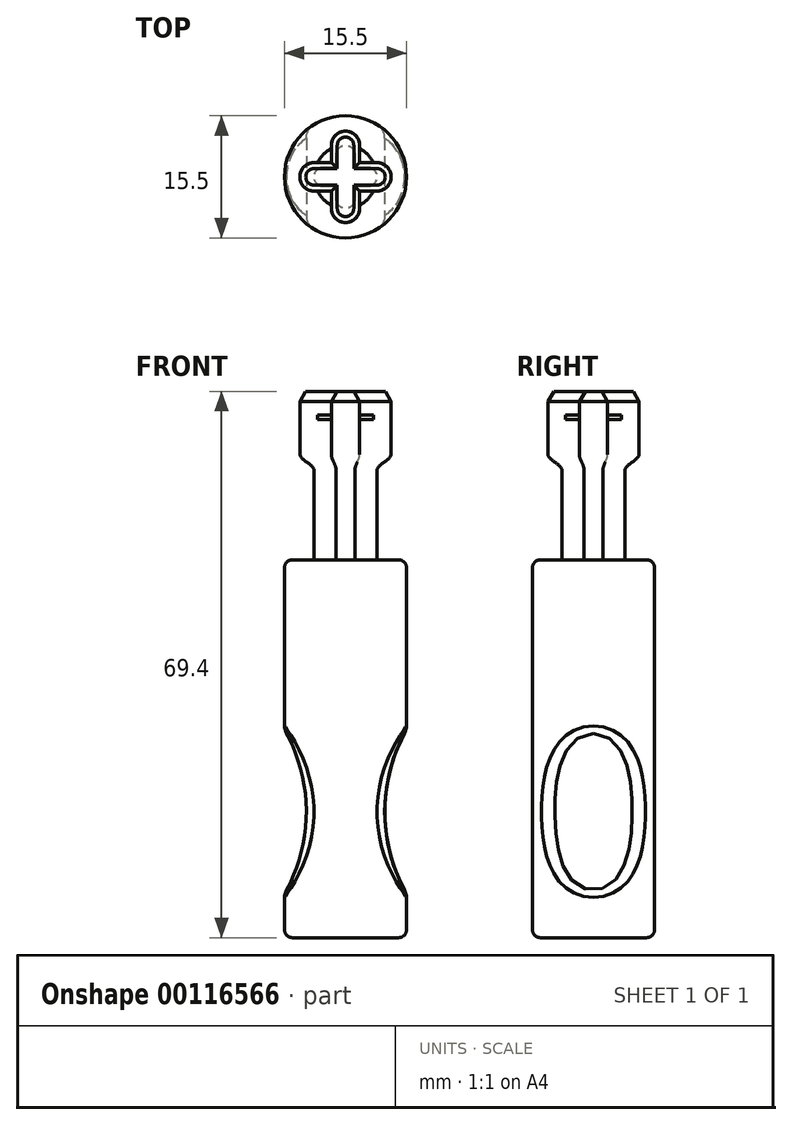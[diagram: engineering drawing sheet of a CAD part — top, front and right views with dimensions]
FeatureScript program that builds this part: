
annotation { "Feature Type Name" : "Feature", "Feature Type Description" : "" }
export const myFeature = defineFeature(function(context is Context, id is Id, definition is map)
    precondition{}
    {
        {
            var Q0;
            Q0=qCreatedBy(makeId("Top.planeOp"),FACE);
            var sketch = newSketch(context, id + "F0", { "sketchPlane" : qUnion([Q0])});
            skCircle(sketch, "E0", {"center": v(0, 0) * mm, "radius": 7.75 * mm});
            skSolve(sketch);
        }
        {
            var Q0;
            Q0=makeQuery(id+"F0.imprint","IMPRINT",FACE,{"disambiguationData":[TD([[makeQuery(id+"F0.imprint","IMPRINT",EDGE,{"derivedFrom":sQuery(id+"F0.wireOp",EDGE,"E0")}),1.0]])]});
            extrude(context, id + "F1", {"entities" : qUnion([Q0]), "depth" : 48 * mm});
        }
        {
            var Q0;
            Q0=makeQuery(id+"F1.opExtrude","CAP_FACE",FACE,{"disambiguationData":[OSD([sQuery(id+"F0.wireOp",EDGE,"E0")])],"isStart":false});
            var sketch = newSketch(context, id + "F2", { "sketchPlane" : qUnion([Q0])});
            skLineSegment(sketch, "E1", {"start": v(2.8, 1.2) * mm, "end": v(1.2, 1.2) * mm});
            skLineSegment(sketch, "E2", {"start": v(1.2, 1.2) * mm, "end": v(1.2, 2.8) * mm});
            skLineSegment(sketch, "E3", {"start": v(-1.2, 2.8) * mm, "end": v(-1.2, 1.2) * mm});
            skLineSegment(sketch, "E4", {"start": v(-1.2, 1.2) * mm, "end": v(-2.8, 1.2) * mm});
            skLineSegment(sketch, "E5", {"start": v(-2.8, -1.2) * mm, "end": v(-1.2, -1.2) * mm});
            skLineSegment(sketch, "E6", {"start": v(-1.2, -1.2) * mm, "end": v(-1.2, -2.8) * mm});
            skLineSegment(sketch, "E7", {"start": v(1.2, -2.8) * mm, "end": v(1.2, -1.2) * mm});
            skLineSegment(sketch, "E8", {"start": v(1.2, -1.2) * mm, "end": v(2.8, -1.2) * mm});
            skArc(sketch, "E9", {"start": v(2.8, 1.2) * mm, "mid": v(4, 0) * mm, "end": v(2.8, -1.2) * mm});
            skArc(sketch, "E10", {"start": v(1.2, 2.8) * mm, "mid": v(0, 4) * mm, "end": v(-1.2, 2.8) * mm});
            skArc(sketch, "E11", {"start": v(-2.8, 1.2) * mm, "mid": v(-4, 0) * mm, "end": v(-2.8, -1.2) * mm});
            skArc(sketch, "E12", {"start": v(-1.2, -2.8) * mm, "mid": v(0, -4) * mm, "end": v(1.2, -2.8) * mm});
            skLineSegment(sketch, "E13", {"start": v(0, 2.8) * mm, "end": v(0, -2.8) * mm, "construction": true});
            skLineSegment(sketch, "E14", {"start": v(-2.8, 0) * mm, "end": v(2.8, 0) * mm, "construction": true});
            skPoint(sketch, "E15", {"position": v(0, 0) * mm});
            skSolve(sketch);
        }
        {
            var Q0;
            Q0=makeQuery(id+"F2.imprint","IMPRINT",FACE,{"disambiguationData":[TD([[makeQuery(id+"F2.imprint","IMPRINT",EDGE,{"derivedFrom":sQuery(id+"F2.wireOp",EDGE,"E1")}),1.0]])]});
            extrude(context, id + "F3", {"entities" : qUnion([Q0]), "operationType" : NewBodyOperationType.ADD, "depth" : 11.4 * mm});
        }
        {
            var Q0;
            Q0=makeQuery(id+"F3.opExtrude","CAP_FACE",FACE,{"disambiguationData":[OSD([sQuery(id+"F2.wireOp",EDGE,"E1"),sQuery(id+"F2.wireOp",EDGE,"E2"),sQuery(id+"F2.wireOp",EDGE,"E3"),sQuery(id+"F2.wireOp",EDGE,"E4"),sQuery(id+"F2.wireOp",EDGE,"E5"),sQuery(id+"F2.wireOp",EDGE,"E6"),sQuery(id+"F2.wireOp",EDGE,"E7"),sQuery(id+"F2.wireOp",EDGE,"E8"),sQuery(id+"F2.wireOp",EDGE,"E9"),sQuery(id+"F2.wireOp",EDGE,"E10"),sQuery(id+"F2.wireOp",EDGE,"E11"),sQuery(id+"F2.wireOp",EDGE,"E12")])],"isStart":false});
            cPlane(context, id + "F4", {"entities" : qUnion([Q0]), "cplaneType" : CPlaneType.OFFSET, "offset" : 2 * mm, "width" : 150 * mm, "height" : 150 * mm});
        }
        {
            var Q0;
            Q0=qCreatedBy(id+"F4.planeOp",FACE);
            var sketch = newSketch(context, id + "F5", { "sketchPlane" : qUnion([Q0])});
            skLineSegment(sketch, "E16", {"start": v(4, 1.8) * mm, "end": v(1.8, 1.8) * mm});
            skLineSegment(sketch, "E17", {"start": v(1.8, 1.8) * mm, "end": v(1.8, 4) * mm});
            skLineSegment(sketch, "E18", {"start": v(-1.8, 4) * mm, "end": v(-1.8, 1.8) * mm});
            skLineSegment(sketch, "E19", {"start": v(-1.8, 1.8) * mm, "end": v(-4, 1.8) * mm});
            skLineSegment(sketch, "E20", {"start": v(-4, -1.8) * mm, "end": v(-1.8, -1.8) * mm});
            skLineSegment(sketch, "E21", {"start": v(-1.8, -1.8) * mm, "end": v(-1.8, -4) * mm});
            skLineSegment(sketch, "E22", {"start": v(1.8, -4) * mm, "end": v(1.8, -1.8) * mm});
            skLineSegment(sketch, "E23", {"start": v(1.8, -1.8) * mm, "end": v(4, -1.8) * mm});
            skArc(sketch, "E24", {"start": v(4, 1.8) * mm, "mid": v(5.8, 0) * mm, "end": v(4, -1.8) * mm});
            skArc(sketch, "E25", {"start": v(1.8, 4) * mm, "mid": v(0, 5.8) * mm, "end": v(-1.8, 4) * mm});
            skArc(sketch, "E26", {"start": v(-4, 1.8) * mm, "mid": v(-5.8, 0) * mm, "end": v(-4, -1.8) * mm});
            skArc(sketch, "E27", {"start": v(-1.8, -4) * mm, "mid": v(0, -5.8) * mm, "end": v(1.8, -4) * mm});
            skLineSegment(sketch, "E28", {"start": v(0, 4) * mm, "end": v(0, -4) * mm, "construction": true});
            skLineSegment(sketch, "E29", {"start": v(-4, 0) * mm, "end": v(4, 0) * mm, "construction": true});
            skPoint(sketch, "E30", {"position": v(0, 0) * mm});
            skSolve(sketch);
        }
        {
            var Q1;
            Q1=makeQuery(id+"F3.opExtrude","CAP_FACE",FACE,{"disambiguationData":[OSD([sQuery(id+"F2.wireOp",EDGE,"E1"),sQuery(id+"F2.wireOp",EDGE,"E2"),sQuery(id+"F2.wireOp",EDGE,"E3"),sQuery(id+"F2.wireOp",EDGE,"E4"),sQuery(id+"F2.wireOp",EDGE,"E5"),sQuery(id+"F2.wireOp",EDGE,"E6"),sQuery(id+"F2.wireOp",EDGE,"E7"),sQuery(id+"F2.wireOp",EDGE,"E8"),sQuery(id+"F2.wireOp",EDGE,"E9"),sQuery(id+"F2.wireOp",EDGE,"E10"),sQuery(id+"F2.wireOp",EDGE,"E11"),sQuery(id+"F2.wireOp",EDGE,"E12")])],"isStart":false});
            var Q2;
            Q2=makeQuery(id+"F5.imprint","IMPRINT",FACE,{"disambiguationData":[TD([[makeQuery(id+"F5.imprint","IMPRINT",EDGE,{"derivedFrom":sQuery(id+"F5.wireOp",EDGE,"E16")}),1.0]])]});
            loft(context, id + "F6", {"operationType" : NewBodyOperationType.ADD, "startCondition" : LoftEndDerivativeType.NORMAL_TO_PROFILE, "startMagnitude" : 1, "endCondition" : LoftEndDerivativeType.NORMAL_TO_PROFILE, "endMagnitude" : 1, "sheetProfilesArray" : [{ "sheetProfileEntities" : qUnion([Q1]) }, { "sheetProfileEntities" : qUnion([Q2]) }]});
        }
        {
            var Q0;
            Q0=makeQuery(id+"F6.opLoft","CAP_FACE",FACE,{"disambiguationData":[OSD([makeQuery(id+"F5.imprint","IMPRINT",FACE,{"disambiguationData":[TD([[makeQuery(id+"F5.imprint","IMPRINT",EDGE,{"derivedFrom":sQuery(id+"F5.wireOp",EDGE,"E16")}),1.0]])]})])],"isStart":true});
            extrude(context, id + "F7", {"entities" : qUnion([Q0]), "operationType" : NewBodyOperationType.ADD, "depth" : 8 * mm});
        }
        {
            var Q0;
            Q0=makeQuery(id+"F7.opExtrude","CAP_EDGE",EDGE,{"disambiguationData":[OSD([sQuery(id+"F5.wireOp",EDGE,"E20"),sQuery(id+"F5.wireOp",EDGE,"E21"),sQuery(id+"F5.wireOp",EDGE,"E27")])],"isStart":false});
            var Q1;
            Q1=makeQuery(id+"F7.opExtrude","CAP_EDGE",EDGE,{"disambiguationData":[OSD([sQuery(id+"F5.wireOp",EDGE,"E17"),sQuery(id+"F5.wireOp",EDGE,"E18"),sQuery(id+"F5.wireOp",EDGE,"E25")])],"isStart":false});
            var Q2;
            Q2=makeQuery(id+"F7.opExtrude","CAP_EDGE",EDGE,{"disambiguationData":[OSD([sQuery(id+"F5.wireOp",EDGE,"E16"),sQuery(id+"F5.wireOp",EDGE,"E17"),sQuery(id+"F5.wireOp",EDGE,"E24")])],"isStart":false});
            var Q3;
            Q3=makeQuery(id+"F7.opExtrude","CAP_EDGE",EDGE,{"disambiguationData":[OSD([sQuery(id+"F5.wireOp",EDGE,"E19"),sQuery(id+"F5.wireOp",EDGE,"E20"),sQuery(id+"F5.wireOp",EDGE,"E26")])],"isStart":false});
            var Q4;
            Q4=makeQuery(id+"F7.opExtrude","CAP_EDGE",EDGE,{"disambiguationData":[OSD([sQuery(id+"F5.wireOp",EDGE,"E18"),sQuery(id+"F5.wireOp",EDGE,"E19"),sQuery(id+"F5.wireOp",EDGE,"E25")])],"isStart":false});
            var Q5;
            Q5=makeQuery(id+"F7.opExtrude","CAP_EDGE",EDGE,{"disambiguationData":[OSD([sQuery(id+"F5.wireOp",EDGE,"E21"),sQuery(id+"F5.wireOp",EDGE,"E22"),sQuery(id+"F5.wireOp",EDGE,"E27")])],"isStart":false});
            var Q6;
            Q6=makeQuery(id+"F7.opExtrude","CAP_EDGE",EDGE,{"disambiguationData":[OSD([sQuery(id+"F5.wireOp",EDGE,"E20"),sQuery(id+"F5.wireOp",EDGE,"E21"),sQuery(id+"F5.wireOp",EDGE,"E26")])],"isStart":false});
            var Q7;
            Q7=makeQuery(id+"F7.opExtrude","CAP_EDGE",EDGE,{"disambiguationData":[OSD([sQuery(id+"F5.wireOp",EDGE,"E16"),sQuery(id+"F5.wireOp",EDGE,"E23"),sQuery(id+"F5.wireOp",EDGE,"E24")])],"isStart":false});
            var Q8;
            Q8=makeQuery(id+"F7.opExtrude","CAP_EDGE",EDGE,{"disambiguationData":[OSD([sQuery(id+"F5.wireOp",EDGE,"E16"),sQuery(id+"F5.wireOp",EDGE,"E17"),sQuery(id+"F5.wireOp",EDGE,"E25")])],"isStart":false});
            var Q9;
            Q9=makeQuery(id+"F7.opExtrude","CAP_EDGE",EDGE,{"disambiguationData":[OSD([sQuery(id+"F5.wireOp",EDGE,"E22"),sQuery(id+"F5.wireOp",EDGE,"E23"),sQuery(id+"F5.wireOp",EDGE,"E27")])],"isStart":false});
            var Q10;
            Q10=makeQuery(id+"F7.opExtrude","CAP_EDGE",EDGE,{"disambiguationData":[OSD([sQuery(id+"F5.wireOp",EDGE,"E18"),sQuery(id+"F5.wireOp",EDGE,"E19"),sQuery(id+"F5.wireOp",EDGE,"E26")])],"isStart":false});
            var Q11;
            Q11=makeQuery(id+"F7.opExtrude","CAP_EDGE",EDGE,{"disambiguationData":[OSD([sQuery(id+"F5.wireOp",EDGE,"E22"),sQuery(id+"F5.wireOp",EDGE,"E23"),sQuery(id+"F5.wireOp",EDGE,"E24")])],"isStart":false});
            chamfer(context, id + "F8", {"entities" : qUnion([Q0, Q1, Q2, Q3, Q4, Q5, Q6, Q7, Q8, Q9, Q10, Q11]), "chamferType" : ChamferType.OFFSET_ANGLE, "width" : 0.75 * mm, "oppositeDirection" : false, "angle" : 60 * degree, "tangentPropagation" : true});
        }
        {
            var Q0;
            Q0=makeQuery(id+"F7.opExtrude","CAP_FACE",FACE,{"disambiguationData":[OSD([makeQuery(id+"F5.imprint","IMPRINT",FACE,{"disambiguationData":[TD([[makeQuery(id+"F5.imprint","IMPRINT",EDGE,{"derivedFrom":sQuery(id+"F5.wireOp",EDGE,"E16")}),1.0]])]})])],"isStart":false});
            cPlane(context, id + "F9", {"entities" : qUnion([Q0]), "cplaneType" : CPlaneType.OFFSET, "offset" : 3 * mm, "oppositeDirection" : true, "width" : 150 * mm, "height" : 150 * mm});
        }
        {
            var Q0;
            Q0=qCreatedBy(id+"F9.planeOp",FACE);
            var sketch = newSketch(context, id + "F10", { "sketchPlane" : qUnion([Q0])});
            skCircle(sketch, "E31", {"center": v(0, 0) * mm, "radius": 4 * mm});
            skSolve(sketch);
        }
        {
            var Q0;
            Q0=makeQuery(id+"F10.imprint","IMPRINT",FACE,{"disambiguationData":[TD([[makeQuery(id+"F10.imprint","IMPRINT",EDGE,{"derivedFrom":sQuery(id+"F10.wireOp",EDGE,"E31")}),1.0]])]});
            extrude(context, id + "F11", {"entities" : qUnion([Q0]), "operationType" : NewBodyOperationType.ADD, "oppositeDirection" : true, "depth" : 0.6 * mm});
        }
        {
            var Q0;
            Q0=qCreatedBy(makeId("Front.planeOp"),FACE);
            var sketch = newSketch(context, id + "F12", { "sketchPlane" : qUnion([Q0])});
            skArc(sketch, "E32", {"start": v(8.77, 28) * mm, "mid": v(4.98, 16) * mm, "end": v(8.77, 4) * mm});
            skLineSegment(sketch, "E33", {"start": v(8.77, 28) * mm, "end": v(8.77, 4) * mm});
            skLineSegment(sketch, "E34", {"start": v(0, -9.33) * mm, "end": v(0, 37.78) * mm, "construction": true});
            skLineSegment(sketch, "E35.MirrorCS", {"start": v(-8.77, 28) * mm, "end": v(-8.77, 4) * mm});
            skArc(sketch, "E36.MirrorCS", {"start": v(-8.77, 28) * mm, "mid": v(-4.98, 16) * mm, "end": v(-8.77, 4) * mm});
            skSolve(sketch);
        }
        {
            var Q0;
            Q0=makeQuery(id+"F12.imprint","IMPRINT",FACE,{"disambiguationData":[TD([[makeQuery(id+"F12.imprint","IMPRINT",EDGE,{"derivedFrom":sQuery(id+"F12.wireOp",EDGE,"E32")}),1.0]])]});
            var Q1;
            Q1=makeQuery(id+"F12.imprint","IMPRINT",FACE,{"disambiguationData":[TD([[makeQuery(id+"F12.imprint","IMPRINT",EDGE,{"derivedFrom":sQuery(id+"F12.wireOp",EDGE,"E35.MirrorCS")}),1.0]])]});
            extrude(context, id + "F13", {"entities" : qUnion([Q0, Q1]), "operationType" : NewBodyOperationType.REMOVE, "endBound" : BoundingType.THROUGH_ALL, "oppositeDirection" : true, "depth" : 25 * mm, "hasSecondDirection" : true, "secondDirectionBound" : SecondDirectionBoundingType.THROUGH_ALL, "secondDirectionOppositeDirection" : false, "secondDirectionDepth" : 25 * mm});
        }
        {
            var Q0;
            Q0=makeQuery(id+"F13.boolean.opBoolean","INTERSECT",EDGE,{"derivedFrom":[makeQuery(id+"F1.opExtrude","SWEPT_FACE",FACE,{"disambiguationData":[OSD([sQuery(id+"F0.wireOp",EDGE,"E0")])]}),makeQuery(id+"F13.opExtrude","SWEPT_FACE",FACE,{"disambiguationData":[OSD([sQuery(id+"F12.wireOp",EDGE,"E36.MirrorCS")])]})]});
            var Q1;
            Q1=makeQuery(id+"F13.boolean.opBoolean","INTERSECT",EDGE,{"derivedFrom":[makeQuery(id+"F1.opExtrude","SWEPT_FACE",FACE,{"disambiguationData":[OSD([sQuery(id+"F0.wireOp",EDGE,"E0")])]}),makeQuery(id+"F13.opExtrude","SWEPT_FACE",FACE,{"disambiguationData":[OSD([sQuery(id+"F12.wireOp",EDGE,"E32")])]})]});
            fillet(context, id + "F14", {"entities" : qUnion([Q0, Q1]), "radius" : 2 * mm, "tangentPropagation" : true, "allowEdgeOverflow" : false});
        }
        {
            var Q0;
            Q0=makeQuery(id+"F1.opExtrude","CAP_EDGE",EDGE,{"disambiguationData":[OSD([sQuery(id+"F0.wireOp",EDGE,"E0")])],"isStart":true});
            var Q1;
            Q1=makeQuery(id+"F1.opExtrude","CAP_EDGE",EDGE,{"disambiguationData":[OSD([sQuery(id+"F0.wireOp",EDGE,"E0")])],"isStart":false});
            fillet(context, id + "F15", {"entities" : qUnion([Q0, Q1]), "radius" : 1 * mm, "tangentPropagation" : true, "allowEdgeOverflow" : false});
        }
    });
